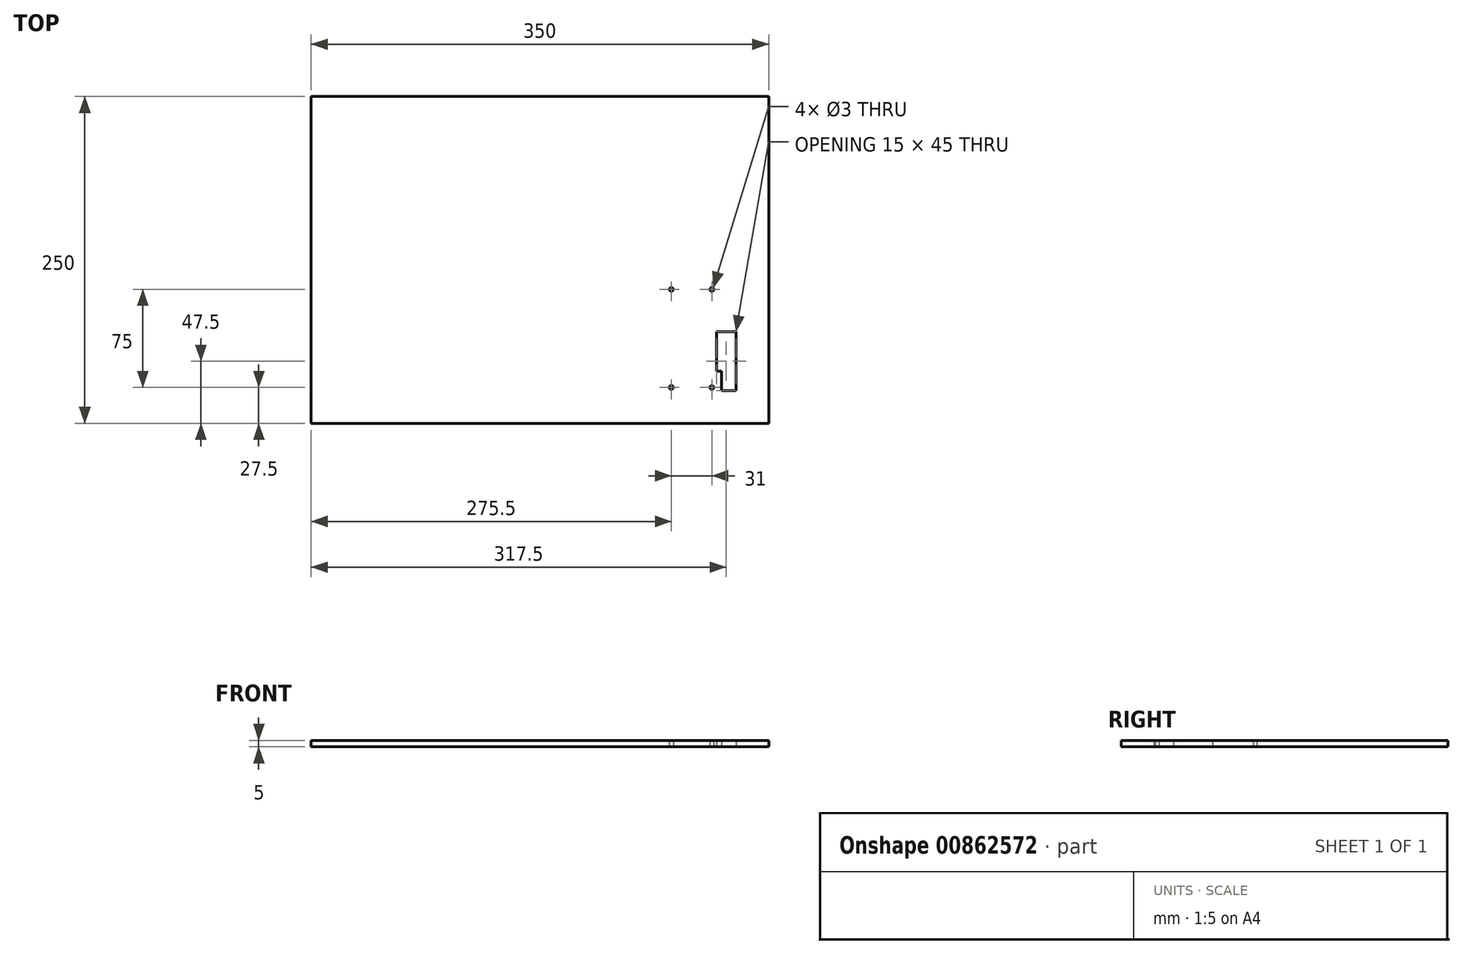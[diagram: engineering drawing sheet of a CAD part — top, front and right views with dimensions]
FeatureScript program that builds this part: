
annotation { "Feature Type Name" : "Feature", "Feature Type Description" : "" }
export const myFeature = defineFeature(function(context is Context, id is Id, definition is map)
    precondition{}
    {
        {
            var Q0;
            Q0=qCreatedBy(makeId("Top.planeOp"),FACE);
            var sketch = newSketch(context, id + "F0", { "sketchPlane" : qUnion([Q0])});
            skLineSegment(sketch, "E0.bottom", {"start": v(175, -125) * mm, "end": v(-175, -125) * mm});
            skLineSegment(sketch, "E0.top", {"start": v(175, 125) * mm, "end": v(-175, 125) * mm});
            skLineSegment(sketch, "E0.left", {"start": v(175, -125) * mm, "end": v(175, 125) * mm});
            skLineSegment(sketch, "E0.right", {"start": v(-175, -125) * mm, "end": v(-175, 125) * mm});
            skPoint(sketch, "E0.middle", {"position": v(0, 0) * mm});
            skLineSegment(sketch, "E1.bottom", {"start": v(135, -55) * mm, "end": v(150, -55) * mm});
            skLineSegment(sketch, "E1.top", {"start": v(139, -100) * mm, "end": v(150, -100) * mm});
            skLineSegment(sketch, "E1.left", {"start": v(135, -55) * mm, "end": v(135, -85) * mm});
            skLineSegment(sketch, "E1.right", {"start": v(150, -55) * mm, "end": v(150, -100) * mm});
            skLineSegment(sketch, "E2", {"start": v(135, -85) * mm, "end": v(139, -85) * mm});
            skLineSegment(sketch, "E3", {"start": v(139, -85) * mm, "end": v(139, -100) * mm});
            skCircle(sketch, "E4", {"center": v(131.5, -97.5) * mm, "radius": 1.5 * mm});
            skCircle(sketch, "E5.0.1.0", {"center": v(131.5, -22.5) * mm, "radius": 1.5 * mm});
            skCircle(sketch, "E5.1.0.0", {"center": v(100.5, -97.5) * mm, "radius": 1.5 * mm});
            skCircle(sketch, "E5.1.1.0", {"center": v(100.5, -22.5) * mm, "radius": 1.5 * mm});
            skLineSegment(sketch, "E5.direction1", {"start": v(131.5, -97.5) * mm, "end": v(100.5, -97.5) * mm, "construction": true});
            skLineSegment(sketch, "E5.direction2", {"start": v(131.5, -97.5) * mm, "end": v(131.5, -22.5) * mm, "construction": true});
            skSolve(sketch);
        }
        {
            var Q0;
            Q0=qSketchRegion(id+"F0",true);
            extrude(context, id + "F1", {"entities" : qUnion([Q0]), "depth" : 5 * mm, "offsetDistance" : 25 * mm});
        }
    });
